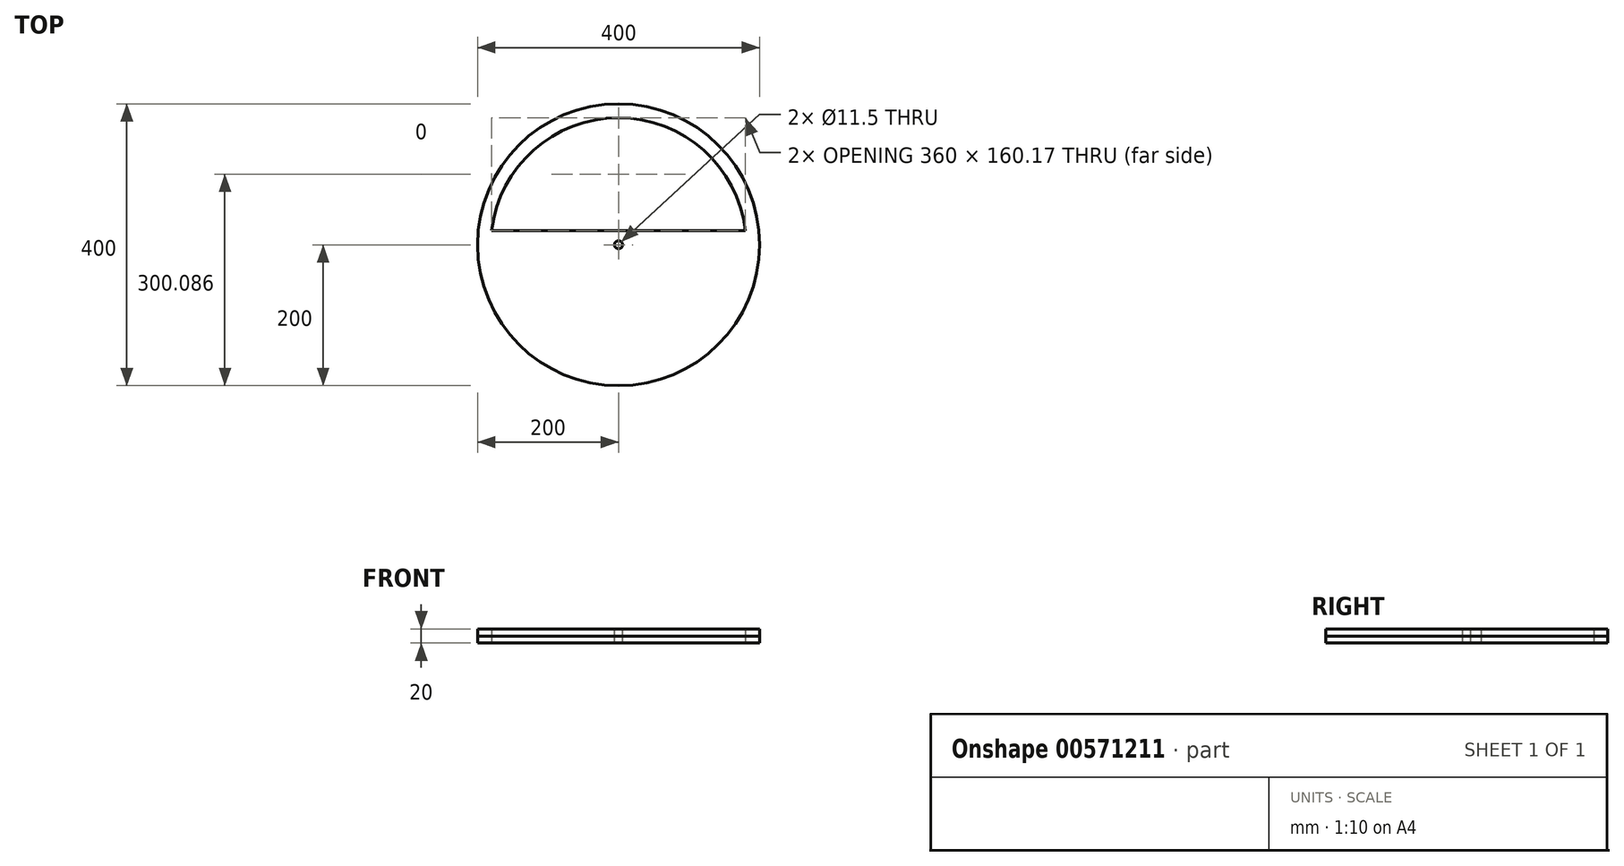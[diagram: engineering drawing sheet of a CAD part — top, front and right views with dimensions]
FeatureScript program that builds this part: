
annotation { "Feature Type Name" : "Feature", "Feature Type Description" : "" }
export const myFeature = defineFeature(function(context is Context, id is Id, definition is map)
    precondition{}
    {
        {
            var Q0;
            Q0=qCreatedBy(makeId("Top.planeOp"),FACE);
            var sketch = newSketch(context, id + "F0", { "sketchPlane" : qUnion([Q0])});
            skCircle(sketch, "E0", {"center": v(0, 0) * mm, "radius": 200 * mm});
            skSolve(sketch);
        }
        {
            var Q0;
            Q0 = qSketchRegion(id + "F0", true);
            extrude(context, id + "F1", {"entities" : qUnion([Q0]), "depth" : 10 * mm, "offsetDistance" : 25.4 * mm});
        }
        {
            var Q0;
            Q0 = qSketchRegion(id + "F0", true);
            extrude(context, id + "F2", {"entities" : qUnion([Q0]), "oppositeDirection" : true, "depth" : 10 * mm, "offsetDistance" : 25.4 * mm});
        }
        {
            var Q0;
            Q0=qCreatedBy(makeId("Top.planeOp"),FACE);
            var sketch = newSketch(context, id + "F3", { "sketchPlane" : qUnion([Q0])});
            skCircle(sketch, "E1", {"center": v(0, 0) * mm, "radius": 5.75 * mm});
            skSolve(sketch);
        }
        {
            var Q0;
            Q0 = qSketchRegion(id + "F3", true);
            extrude(context, id + "F4", {"entities" : qUnion([Q0]), "operationType" : NewBodyOperationType.REMOVE, "oppositeDirection" : true, "depth" : 10 * mm, "offsetDistance" : 25.4 * mm, "hasSecondDirection" : true, "secondDirectionOppositeDirection" : false, "secondDirectionDepth" : 20 * mm});
        }
        {
            var Q0;
            Q0=qCreatedBy(makeId("Top.planeOp"),FACE);
            var sketch = newSketch(context, id + "F5", { "sketchPlane" : qUnion([Q0])});
            skArc(sketch, "E2", {"start": v(180, 20) * mm, "mid": v(0, 180.17) * mm, "end": v(-180, 20) * mm});
            skLineSegment(sketch, "E3", {"start": v(-180, 20) * mm, "end": v(180, 20) * mm});
            skSolve(sketch);
        }
        {
            var Q0;
            Q0 = qSketchRegion(id + "F5", true);
            extrude(context, id + "F6", {"entities" : qUnion([Q0]), "operationType" : NewBodyOperationType.REMOVE, "depth" : 10 * mm, "offsetDistance" : 25.4 * mm, "hasSecondDirection" : true, "secondDirectionOppositeDirection" : true, "secondDirectionDepth" : 10 * mm});
        }
    });
